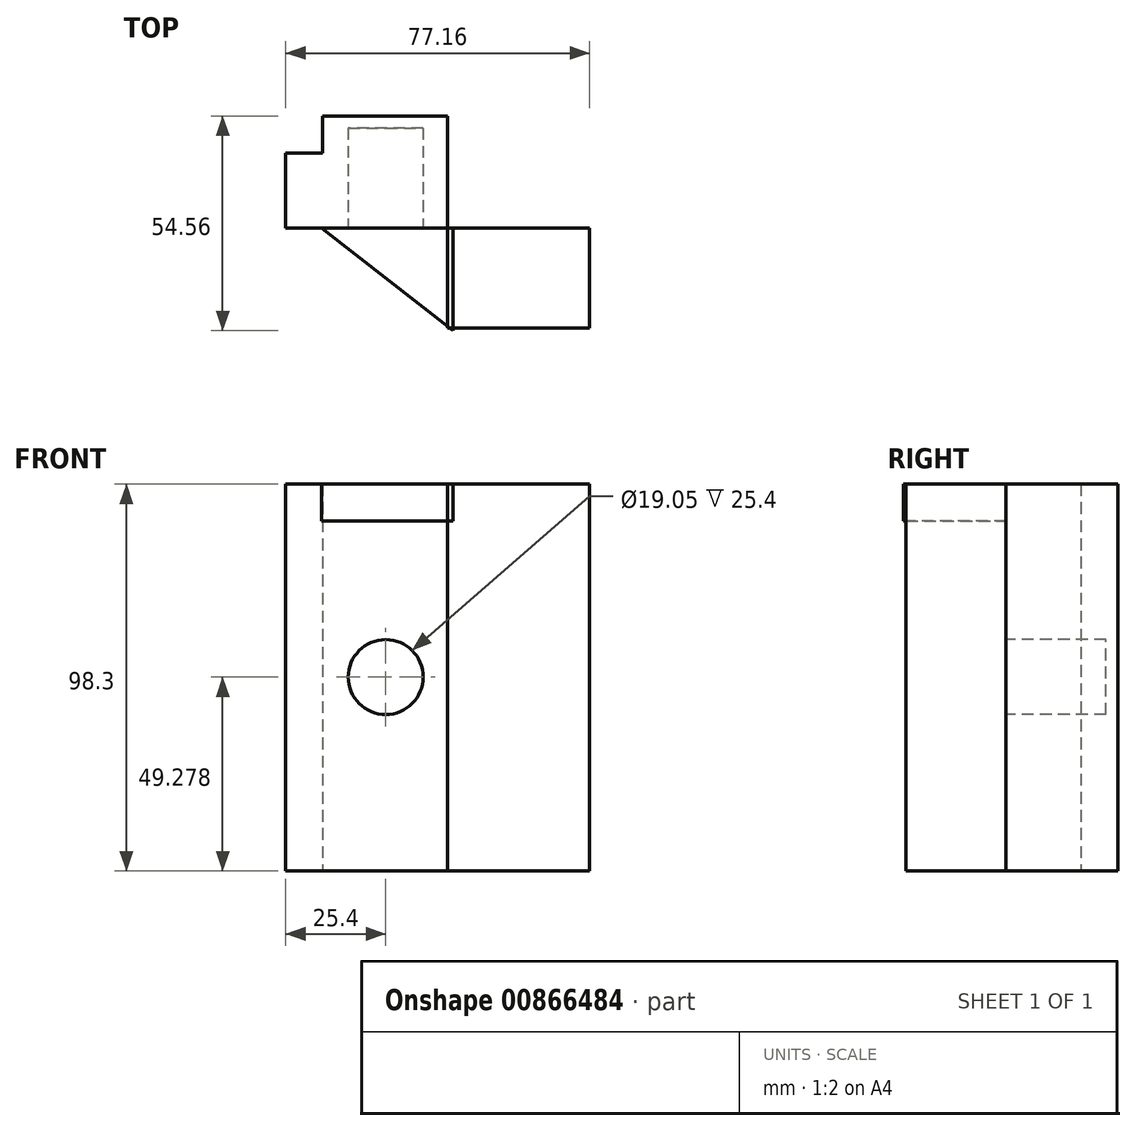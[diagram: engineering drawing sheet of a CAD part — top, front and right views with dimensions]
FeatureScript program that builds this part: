
annotation { "Feature Type Name" : "Feature", "Feature Type Description" : "" }
export const myFeature = defineFeature(function(context is Context, id is Id, definition is map)
    precondition{}
    {
        {
            var Q0;
            Q0=qCreatedBy(makeId("Front.planeOp"),FACE);
            var sketch = newSketch(context, id + "F0", { "sketchPlane" : qUnion([Q0])});
            skLineSegment(sketch, "E0.bottom", {"start": v(0, 0) * mm, "end": v(41.15, 0) * mm});
            skLineSegment(sketch, "E0.top", {"start": v(0, -98.3) * mm, "end": v(41.15, -98.3) * mm});
            skLineSegment(sketch, "E0.left", {"start": v(0, 0) * mm, "end": v(0, -98.3) * mm});
            skLineSegment(sketch, "E0.right", {"start": v(41.15, 0) * mm, "end": v(41.15, -98.3) * mm});
            skSolve(sketch);
        }
        {
            var Q0;
            Q0 = qSketchRegion(id + "F0", true);
            extrude(context, id + "F1", {"entities" : qUnion([Q0]), "oppositeDirection" : true, "depth" : 19.05 * mm, "offsetDistance" : 25.4 * mm});
        }
        {
            var Q0;
            Q0=makeQuery(id+"F1.opExtrude","CAP_FACE",FACE,{"disambiguationData":[OSD([sQuery(id+"F0.wireOp",EDGE,"E0.bottom"),sQuery(id+"F0.wireOp",EDGE,"E0.top"),sQuery(id+"F0.wireOp",EDGE,"E0.left"),sQuery(id+"F0.wireOp",EDGE,"E0.right")])],"isStart":false});
            var sketch = newSketch(context, id + "F2", { "sketchPlane" : qUnion([Q0])});
            skLineSegment(sketch, "E1", {"start": v(-9.4, 0) * mm, "end": v(-9.4, -98.3) * mm});
            skLineSegment(sketch, "E2", {"start": v(-9.4, -98.3) * mm, "end": v(-41.15, -98.3) * mm});
            skLineSegment(sketch, "E3", {"start": v(-41.15, -98.3) * mm, "end": v(-41.15, 0) * mm});
            skLineSegment(sketch, "E4", {"start": v(-41.15, 0) * mm, "end": v(-9.4, 0) * mm});
            skSolve(sketch);
        }
        {
            var Q0;
            Q0=makeQuery(id+"F2.imprint","IMPRINT",FACE,{"disambiguationData":[TD([[makeQuery(id+"F2.imprint","IMPRINT",EDGE,{"derivedFrom":sQuery(id+"F2.wireOp",EDGE,"E1")}),-1.0]])]});
            extrude(context, id + "F3", {"entities" : qUnion([Q0]), "operationType" : NewBodyOperationType.ADD, "depth" : 9.4 * mm, "offsetDistance" : 25.4 * mm});
        }
        {
            var Q0;
            Q0=makeQuery(id+"F1.opExtrude","CAP_FACE",FACE,{"disambiguationData":[OSD([sQuery(id+"F0.wireOp",EDGE,"E0.bottom"),sQuery(id+"F0.wireOp",EDGE,"E0.top"),sQuery(id+"F0.wireOp",EDGE,"E0.left"),sQuery(id+"F0.wireOp",EDGE,"E0.right")])],"isStart":true});
            var sketch = newSketch(context, id + "F4", { "sketchPlane" : qUnion([Q0])});
            skCircle(sketch, "E5", {"center": v(25.4, -49.02) * mm, "radius": 9.53 * mm});
            skSolve(sketch);
        }
        {
            var Q0;
            Q0=makeQuery(id+"F4.imprint","IMPRINT",FACE,{"disambiguationData":[TD([[makeQuery(id+"F4.imprint","IMPRINT",EDGE,{"derivedFrom":sQuery(id+"F4.wireOp",EDGE,"E5")}),1.0]])]});
            extrude(context, id + "F5", {"entities" : qUnion([Q0]), "operationType" : NewBodyOperationType.REMOVE, "oppositeDirection" : true, "depth" : 25.4 * mm, "offsetDistance" : 25.4 * mm});
        }
        {
            var Q0;
            Q0=makeQuery(id+"F1.opExtrude","CAP_FACE",FACE,{"disambiguationData":[OSD([sQuery(id+"F0.wireOp",EDGE,"E0.bottom"),sQuery(id+"F0.wireOp",EDGE,"E0.top"),sQuery(id+"F0.wireOp",EDGE,"E0.left"),sQuery(id+"F0.wireOp",EDGE,"E0.right")])],"isStart":true});
            var sketch = newSketch(context, id + "F6", { "sketchPlane" : qUnion([Q0])});
            skLineSegment(sketch, "E6", {"start": v(8.97, 0) * mm, "end": v(8.97, -9.4) * mm});
            skLineSegment(sketch, "E7", {"start": v(8.97, -9.4) * mm, "end": v(41.15, -9.4) * mm});
            skLineSegment(sketch, "E8", {"start": v(41.15, -9.4) * mm, "end": v(41.15, 0) * mm});
            skLineSegment(sketch, "E9", {"start": v(41.15, 0) * mm, "end": v(8.97, 0) * mm});
            skLineSegment(sketch, "E10", {"start": v(41.15, 0) * mm, "end": v(77.16, 0) * mm});
            skLineSegment(sketch, "E11", {"start": v(77.16, 0) * mm, "end": v(77.16, -98.3) * mm});
            skLineSegment(sketch, "E12", {"start": v(77.16, -98.3) * mm, "end": v(41.15, -98.3) * mm});
            skLineSegment(sketch, "E13", {"start": v(41.15, -88.9) * mm, "end": v(8.97, -88.9) * mm});
            skLineSegment(sketch, "E14", {"start": v(8.97, -88.9) * mm, "end": v(8.97, -98.3) * mm});
            skSolve(sketch);
        }
        {
            var Q0;
            {var subQ1=sQuery(id+"F6.wireOp",EDGE,"E8");Q0=makeQuery(id+"F6.imprint","IMPRINT",FACE,{"disambiguationData":[TD([[makeQuery(id+"F6.imprint","IMPRINT",EDGE,{"derivedFrom":subQ1}),1.0]])]});}
            extrude(context, id + "F7", {"entities" : qUnion([Q0]), "depth" : 25.4 * mm, "offsetDistance" : 25.4 * mm});
        }
        {
            var Q0;
            Q0=qCreatedBy(makeId("Top.planeOp"),FACE);
            var sketch = newSketch(context, id + "F8", { "sketchPlane" : qUnion([Q0])});
            skLineSegment(sketch, "E15", {"start": v(42.44, -26.1) * mm, "end": v(42.44, 0) * mm});
            skLineSegment(sketch, "E16", {"start": v(42.44, 0) * mm, "end": v(9.15, 0) * mm});
            skLineSegment(sketch, "E17", {"start": v(9.15, 0) * mm, "end": v(42.44, -26.1) * mm});
            skSolve(sketch);
        }
        {
            var Q0;
            Q0 = qSketchRegion(id + "F8", true);
            extrude(context, id + "F9", {"entities" : qUnion([Q0]), "oppositeDirection" : true, "depth" : 9.4 * mm, "offsetDistance" : 25.4 * mm});
        }
    });
